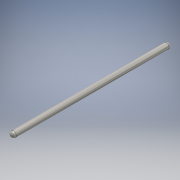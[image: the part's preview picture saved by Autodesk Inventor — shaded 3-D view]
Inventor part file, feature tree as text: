
AUTODESK INVENTOR PART (.ipt)
format: ipt  version: 2016 (Build 200138000, 138)  size: 107,008 bytes
history: native  units: mm
features: fillet x2, extrude x1, sketch x1
ambient origin geometry x8: Origin, YZ Plane, XZ Plane, XY Plane, X Axis, Y Axis, Z Axis, Center Point
bodies: Solid1 (feature_tree)
feature tree (4):
  extrude  "Extrusion1"  Depth=0.5mm TaperAngle=0.0deg
  fillet  "Fillet1"  Radius=0.5mm
  fillet  "Fillet2"  Radius=0.5mm
  sketch  "Sketch1"  dims[d0=1.0mm d1=28.0mm d2=0.0mm d3=0.5mm d4=0.5mm]
